annotation { "Feature Type Name" : "Feature", "Feature Type Description" : "" }
export const myFeature = defineFeature(function(context is Context, id is Id, definition is map)
    precondition{}
    {
        {
            var Q0;
            Q0=qCreatedBy(makeId("Front.planeOp"),FACE);
            var sketch = newSketch(context, id + "F0", { "sketchPlane" : qUnion([Q0])});
            skLineSegment(sketch, "E0.bottom", {"start": v(-5.31, 3.25) * mm, "end": v(8.02, 3.25) * mm});
            skLineSegment(sketch, "E0.top", {"start": v(-5.31, -3.25) * mm, "end": v(8.02, -3.25) * mm});
            skLineSegment(sketch, "E0.left", {"start": v(-5.31, 3.25) * mm, "end": v(-5.31, -3.25) * mm});
            skLineSegment(sketch, "E0.right", {"start": v(8.02, 3.25) * mm, "end": v(8.02, -3.25) * mm});
            skArc(sketch, "E1", {"start": v(-5.31, 3.25) * mm, "mid": v(-8.56, 0) * mm, "end": v(-5.31, -3.25) * mm});
            skArc(sketch, "E2", {"start": v(8.02, -3.25) * mm, "mid": v(11.27, 0) * mm, "end": v(8.02, 3.25) * mm});
            skLineSegment(sketch, "E3.0", {"start": v(-5.31, 5.26) * mm, "end": v(8.02, 5.26) * mm});
            skArc(sketch, "E3.1", {"start": v(-5.31, 5.26) * mm, "mid": v(-10.57, 0) * mm, "end": v(-5.31, -5.26) * mm});
            skLineSegment(sketch, "E3.2", {"start": v(-5.31, -5.26) * mm, "end": v(8.02, -5.26) * mm});
            skArc(sketch, "E3.3", {"start": v(8.02, -5.26) * mm, "mid": v(13.28, 0) * mm, "end": v(8.02, 5.26) * mm});
            skSolve(sketch);
        }
        {
            var Q0;
            Q0=makeQuery(id+"F0.imprint","IMPRINT",FACE,{"disambiguationData":[TD([[makeQuery(id+"F0.imprint","IMPRINT",EDGE,{"derivedFrom":sQuery(id+"F0.wireOp",EDGE,"E0.bottom")}),1.0]])]});
            extrude(context, id + "F1", {"entities" : qUnion([Q0]), "depth" : 55.88 * mm});
        }
        {
            var Q0;
            Q0=makeQuery(id+"F1.opExtrude","CAP_FACE",FACE,{"disambiguationData":[OSD([sQuery(id+"F0.wireOp",EDGE,"E0.bottom"),sQuery(id+"F0.wireOp",EDGE,"E0.top"),sQuery(id+"F0.wireOp",EDGE,"E1"),sQuery(id+"F0.wireOp",EDGE,"E2"),sQuery(id+"F0.wireOp",EDGE,"E3.0"),sQuery(id+"F0.wireOp",EDGE,"E3.1"),sQuery(id+"F0.wireOp",EDGE,"E3.2"),sQuery(id+"F0.wireOp",EDGE,"E3.3")])],"isStart":false});
            var sketch = newSketch(context, id + "F2", { "sketchPlane" : qUnion([Q0])});
            skLineSegment(sketch, "E4.bottom", {"start": v(-12.38, 7.2) * mm, "end": v(15.59, 7.2) * mm});
            skLineSegment(sketch, "E4.top", {"start": v(-12.38, 2.53) * mm, "end": v(15.59, 2.53) * mm});
            skLineSegment(sketch, "E4.left", {"start": v(-12.38, 7.2) * mm, "end": v(-12.38, 2.53) * mm});
            skLineSegment(sketch, "E4.right", {"start": v(15.59, 7.2) * mm, "end": v(15.59, 2.53) * mm});
            skSolve(sketch);
        }
        {
            var Q0;
            Q0 = qSketchRegion(id + "F2", true);
            extrude(context, id + "F3", {"entities" : qUnion([Q0]), "operationType" : NewBodyOperationType.REMOVE, "oppositeDirection" : true, "depth" : 55.88 * mm});
        }
        {
            var Q0;
            Q0=makeQuery(id+"F1.opExtrude","SWEPT_FACE",FACE,{"disambiguationData":[OSD([sQuery(id+"F0.wireOp",EDGE,"E3.2")])]});
            var sketch = newSketch(context, id + "F4", { "sketchPlane" : qUnion([Q0])});
            skText(sketch, "E5", { "text": "Vape Naysh", "fontName": "OpenSans-Regular.ttf"});
            const initialGuessF4  = {"E5": [-0.00178, 0.05391, 0, -1, 0.00668]};
            skSetInitialGuess(sketch, initialGuessF4);
            skSolve(sketch);
        }
        {
            var Q0;
            Q0 = qSketchRegion(id + "F4", true);
            extrude(context, id + "F5", {"entities" : qUnion([Q0]), "operationType" : NewBodyOperationType.REMOVE, "oppositeDirection" : true, "depth" : 25.4 * mm});
        }
        {
            var Q0;
            {var subQ1=sQuery(id+"F0.wireOp",EDGE,"E3.2");var subQ2=sQuery(id+"F0.wireOp",EDGE,"E3.1");Q0=makeQuery(id+"F5.boolean.opBoolean","SPLIT",FACE,{"disambiguationData":[TD([makeQuery(id+"F1.opExtrude","SWEPT_FACE",FACE,{"disambiguationData":[OSD([subQ2])]})])],"derivedFrom":makeQuery(id+"F1.opExtrude","SWEPT_FACE",FACE,{"disambiguationData":[OSD([subQ1])]})});}
            var sketch = newSketch(context, id + "F6", { "sketchPlane" : qUnion([Q0])});
            skLineSegment(sketch, "E6.bottom", {"start": v(1.17, 46.6) * mm, "end": v(-3.1, 46.6) * mm});
            skLineSegment(sketch, "E6.top", {"start": v(1.17, 46.39) * mm, "end": v(-3.1, 46.39) * mm});
            skLineSegment(sketch, "E6.left", {"start": v(1.17, 46.6) * mm, "end": v(1.17, 46.39) * mm});
            skLineSegment(sketch, "E6.right", {"start": v(-3.1, 46.6) * mm, "end": v(-3.1, 46.39) * mm});
            skFitSpline(sketch, "E7.0", {"points": [v(0.63, 45.49) * mm, v(0.6, 46.38) * mm, v(0.35, 46.78) * mm]});
            skFitSpline(sketch, "E8.0", {"points": [v(-1.03, 46.93) * mm, v(-1.25, 46.68) * mm, v(-1.25, 46.24) * mm]});
            skSolve(sketch);
        }
        {
            var Q0;
            {var subQ0=sQuery(id+"F6.wireOp",EDGE,"E7.0");var subQ1=sQuery(id+"F6.wireOp",EDGE,"E6.bottom");var subQ2=makeQuery(id+"F6.imprint","INTERSECT",VERTEX,{"derivedFrom":[subQ1,subQ0]});Q0=makeQuery(id+"F6.imprint","IMPRINT",FACE,{"disambiguationData":[TD([[makeQuery(id+"F6.imprint","IMPRINT",EDGE,{"disambiguationData":[TD([[subQ2,1.0]])],"derivedFrom":subQ1}),1.0]])]});}
            var Q1;
            {var subQ0=sQuery(id+"F6.wireOp",EDGE,"E8.0");var subQ1=sQuery(id+"F6.wireOp",EDGE,"E6.bottom");var subQ2=makeQuery(id+"F6.imprint","INTERSECT",VERTEX,{"derivedFrom":[subQ1,subQ0]});Q1=makeQuery(id+"F6.imprint","IMPRINT",FACE,{"disambiguationData":[TD([[makeQuery(id+"F6.imprint","IMPRINT",EDGE,{"disambiguationData":[TD([[subQ2,-1.0]])],"derivedFrom":subQ1}),1.0]])]});}
            var Q2;
            Q2=makeQuery(id+"F5.boolean.opBoolean","SPLIT",FACE,{"disambiguationData":[TD([makeQuery(id+"F5.opExtrude","SWEPT_FACE",FACE,{"disambiguationData":[OSD([sQuery(id+"F4.wireOp",EDGE,"E5.sketch_text.stroke-28")])]})])],"derivedFrom":makeQuery(id+"F1.opExtrude","SWEPT_FACE",FACE,{"disambiguationData":[OSD([sQuery(id+"F0.wireOp",EDGE,"E0.top")])]})});
            extrude(context, id + "F7", {"entities" : qUnion([Q0, Q1]), "operationType" : NewBodyOperationType.ADD, "endBound" : BoundingType.UP_TO_SURFACE, "oppositeDirection" : true, "endBoundEntityFace" : qUnion([Q2]), "depth" : 25.4 * mm});
        }
        {
            var Q0;
            Q0=makeQuery(id+"F5.boolean.opBoolean","SPLIT",FACE,{"disambiguationData":[TD([makeQuery(id+"F5.opExtrude","SWEPT_FACE",FACE,{"disambiguationData":[OSD([sQuery(id+"F4.wireOp",EDGE,"E5.sketch_text.stroke-52")])]})])],"derivedFrom":makeQuery(id+"F1.opExtrude","SWEPT_FACE",FACE,{"disambiguationData":[OSD([sQuery(id+"F0.wireOp",EDGE,"E3.2")])]})});
            var sketch = newSketch(context, id + "F8", { "sketchPlane" : qUnion([Q0])});
            skLineSegment(sketch, "E9.bottom", {"start": v(3.44, 40.97) * mm, "end": v(-2.3, 40.97) * mm});
            skLineSegment(sketch, "E9.top", {"start": v(3.44, 40.66) * mm, "end": v(-2.3, 40.66) * mm});
            skLineSegment(sketch, "E9.left", {"start": v(3.44, 40.97) * mm, "end": v(3.44, 40.66) * mm});
            skLineSegment(sketch, "E9.right", {"start": v(-2.3, 40.97) * mm, "end": v(-2.3, 40.66) * mm});
            skSolve(sketch);
        }
        {
            var Q0;
            {var subQ0=sQuery(id+"F8.wireOp",EDGE,"E9.right");Q0=makeQuery(id+"F8.imprint","IMPRINT",FACE,{"disambiguationData":[TD([[makeQuery(id+"F8.imprint","IMPRINT",EDGE,{"derivedFrom":subQ0}),1.0]])]});}
            var Q1;
            {var subQ0=sQuery(id+"F8.wireOp",EDGE,"E9.left");Q1=makeQuery(id+"F8.imprint","IMPRINT",FACE,{"disambiguationData":[TD([[makeQuery(id+"F8.imprint","IMPRINT",EDGE,{"derivedFrom":subQ0}),-1.0]])]});}
            extrude(context, id + "F9", {"entities" : qUnion([Q0, Q1]), "operationType" : NewBodyOperationType.ADD, "oppositeDirection" : true, "depth" : 2 * mm});
        }
        {
            var Q0;
            {var subQ0=sQuery(id+"F4.wireOp",EDGE,"E5.sketch_text.stroke-68");var subQ1=sQuery(id+"F4.wireOp",EDGE,"E5.sketch_text.stroke-65");var subQ2=sQuery(id+"F4.wireOp",EDGE,"E5.sketch_text.stroke-64");var subQ3=sQuery(id+"F8.wireOp",EDGE,"E9.top");var subQ4=sQuery(id+"F8.wireOp",EDGE,"E9.bottom");var subQ5=sQuery(id+"F4.wireOp",EDGE,"E5.sketch_text.stroke-56");var subQ6=sQuery(id+"F4.wireOp",EDGE,"E5.sketch_text.stroke-52");var subQ7=sQuery(id+"F6.wireOp",EDGE,"E6.top");var subQ8=sQuery(id+"F6.wireOp",EDGE,"E6.bottom");var subQ9=sQuery(id+"F4.wireOp",EDGE,"E5.sketch_text.stroke-13");var subQ10=sQuery(id+"F4.wireOp",EDGE,"E5.sketch_text.stroke-15");var subQ11=sQuery(id+"F0.wireOp",EDGE,"E3.2");var subQ12=makeQuery(id+"F1.opExtrude","SWEPT_FACE",FACE,{"disambiguationData":[OSD([subQ11])]});var subQ14=sQuery(id+"F0.wireOp",EDGE,"E3.1");Q0=makeQuery(id+"FvCUFkXDUsI6DTU_1.boolean.opBoolean","MERGE",FACE,{"derivedFrom":[makeQuery(id+"F5.boolean.opBoolean","SPLIT",FACE,{"disambiguationData":[TD([makeQuery(id+"F5.opExtrude","SWEPT_FACE",FACE,{"disambiguationData":[OSD([sQuery(id+"F4.wireOp",EDGE,"E5.sketch_text.stroke-75")])]})])],"derivedFrom":subQ12}),makeQuery(id+"F9.boolean.opBoolean","MERGE",FACE,{"derivedFrom":[makeQuery(id+"F5.boolean.opBoolean","SPLIT",FACE,{"disambiguationData":[TD([makeQuery(id+"F5.opExtrude","SWEPT_FACE",FACE,{"disambiguationData":[OSD([subQ6])]})])],"derivedFrom":subQ12}),makeQuery(id+"F7.boolean.opBoolean","MERGE",FACE,{"derivedFrom":[makeQuery(id+"F5.boolean.opBoolean","SPLIT",FACE,{"disambiguationData":[TD([makeQuery(id+"F1.opExtrude","SWEPT_FACE",FACE,{"disambiguationData":[OSD([subQ14])]})])],"derivedFrom":subQ12}),makeQuery(id+"F5.boolean.opBoolean","SPLIT",FACE,{"disambiguationData":[TD([makeQuery(id+"F5.opExtrude","SWEPT_FACE",FACE,{"disambiguationData":[OSD([sQuery(id+"F4.wireOp",EDGE,"E5.sketch_text.stroke-28")])]})])],"derivedFrom":subQ12}),makeQuery(id+"F7.opExtrude","CAP_FACE",FACE,{"disambiguationData":[OSD([subQ10,subQ8,subQ7,sQuery(id+"F6.wireOp",EDGE,"E7.0")])],"isStart":true}),makeQuery(id+"F7.opExtrude","CAP_FACE",FACE,{"disambiguationData":[OSD([subQ9,subQ8,subQ7,sQuery(id+"F6.wireOp",EDGE,"E8.0")])],"isStart":true})]}),makeQuery(id+"F9.opExtrude","CAP_FACE",FACE,{"disambiguationData":[OSD([subQ6,subQ4,subQ3,sQuery(id+"F8.wireOp",EDGE,"E9.left")])],"isStart":true}),makeQuery(id+"F9.opExtrude","CAP_FACE",FACE,{"disambiguationData":[OSD([subQ5,subQ4,subQ3,sQuery(id+"F8.wireOp",EDGE,"E9.right")])],"isStart":true})]}),makeQuery(id+"FvCUFkXDUsI6DTU_1.opExtrude","CAP_FACE",FACE,{"disambiguationData":[OSD([subQ2,subQ1,subQ0,sQuery(id+"FhZDdOnHOzzq7TN_1.wireOp",EDGE,"bsYgK6K2-3tY7-JA5x-VERg-xGbtDLP8pClo.bottom"),sQuery(id+"FhZDdOnHOzzq7TN_1.wireOp",EDGE,"bsYgK6K2-3tY7-JA5x-VERg-xGbtDLP8pClo.top")])],"isStart":true})]});}
            var sketch = newSketch(context, id + "F10", { "sketchPlane" : qUnion([Q0])});
            skLineSegment(sketch, "E10.bottom", {"start": v(1.56, 20.76) * mm, "end": v(-2.41, 20.76) * mm});
            skLineSegment(sketch, "E10.top", {"start": v(1.56, 20.47) * mm, "end": v(-2.41, 20.47) * mm});
            skLineSegment(sketch, "E10.left", {"start": v(1.56, 20.76) * mm, "end": v(1.56, 20.47) * mm});
            skLineSegment(sketch, "E10.right", {"start": v(-2.41, 20.76) * mm, "end": v(-2.41, 20.47) * mm});
            skSolve(sketch);
        }
        {
            var Q0;
            {var subQ0=sQuery(id+"F10.wireOp",EDGE,"E10.bottom");var subQ1=makeQuery(id+"F5.boolean.opBoolean","COPY",EDGE,{"derivedFrom":makeQuery(id+"F5.opExtrude","CAP_EDGE",EDGE,{"disambiguationData":[OSD([sQuery(id+"F4.wireOp",EDGE,"E5.sketch_text.stroke-101")])],"isStart":true})});var subQ2=makeQuery(id+"F10.imprint","INTERSECT",VERTEX,{"derivedFrom":[subQ1,subQ0]});Q0=makeQuery(id+"F10.imprint","IMPRINT",FACE,{"disambiguationData":[TD([[makeQuery(id+"F10.imprint","IMPRINT",EDGE,{"disambiguationData":[TD([[subQ2,-1.0]])],"derivedFrom":subQ0}),1.0]])]});}
            extrude(context, id + "F11", {"entities" : qUnion([Q0]), "operationType" : NewBodyOperationType.ADD, "oppositeDirection" : true, "depth" : 2 * mm});
        }
        {
            var Q0;
            {var subQ0=sQuery(id+"F4.wireOp",EDGE,"E5.sketch_text.stroke-101");var subQ1=sQuery(id+"F4.wireOp",EDGE,"E5.sketch_text.stroke-98");var subQ2=sQuery(id+"F8.wireOp",EDGE,"E9.top");var subQ3=sQuery(id+"F8.wireOp",EDGE,"E9.bottom");var subQ4=sQuery(id+"F4.wireOp",EDGE,"E5.sketch_text.stroke-56");var subQ5=sQuery(id+"F4.wireOp",EDGE,"E5.sketch_text.stroke-52");var subQ6=sQuery(id+"F6.wireOp",EDGE,"E6.top");var subQ7=sQuery(id+"F6.wireOp",EDGE,"E6.bottom");var subQ8=sQuery(id+"F4.wireOp",EDGE,"E5.sketch_text.stroke-13");var subQ9=sQuery(id+"F4.wireOp",EDGE,"E5.sketch_text.stroke-15");var subQ10=sQuery(id+"F0.wireOp",EDGE,"E3.2");var subQ11=makeQuery(id+"F1.opExtrude","SWEPT_FACE",FACE,{"disambiguationData":[OSD([subQ10])]});var subQ13=sQuery(id+"F0.wireOp",EDGE,"E3.1");Q0=makeQuery(id+"F11.boolean.opBoolean","MERGE",FACE,{"derivedFrom":[makeQuery(id+"F5.boolean.opBoolean","SPLIT",FACE,{"disambiguationData":[TD([makeQuery(id+"F5.opExtrude","SWEPT_FACE",FACE,{"disambiguationData":[OSD([sQuery(id+"F4.wireOp",EDGE,"E5.sketch_text.stroke-114")])]})])],"derivedFrom":subQ11}),makeQuery(id+"F9.boolean.opBoolean","MERGE",FACE,{"derivedFrom":[makeQuery(id+"F5.boolean.opBoolean","SPLIT",FACE,{"disambiguationData":[TD([makeQuery(id+"F5.opExtrude","SWEPT_FACE",FACE,{"disambiguationData":[OSD([subQ5])]})])],"derivedFrom":subQ11}),makeQuery(id+"F7.boolean.opBoolean","MERGE",FACE,{"derivedFrom":[makeQuery(id+"F5.boolean.opBoolean","SPLIT",FACE,{"disambiguationData":[TD([makeQuery(id+"F1.opExtrude","SWEPT_FACE",FACE,{"disambiguationData":[OSD([subQ13])]})])],"derivedFrom":subQ11}),makeQuery(id+"F5.boolean.opBoolean","SPLIT",FACE,{"disambiguationData":[TD([makeQuery(id+"F5.opExtrude","SWEPT_FACE",FACE,{"disambiguationData":[OSD([sQuery(id+"F4.wireOp",EDGE,"E5.sketch_text.stroke-28")])]})])],"derivedFrom":subQ11}),makeQuery(id+"F7.opExtrude","CAP_FACE",FACE,{"disambiguationData":[OSD([subQ9,subQ7,subQ6,sQuery(id+"F6.wireOp",EDGE,"E7.0")])],"isStart":true}),makeQuery(id+"F7.opExtrude","CAP_FACE",FACE,{"disambiguationData":[OSD([subQ8,subQ7,subQ6,sQuery(id+"F6.wireOp",EDGE,"E8.0")])],"isStart":true})]}),makeQuery(id+"F9.opExtrude","CAP_FACE",FACE,{"disambiguationData":[OSD([subQ5,subQ3,subQ2,sQuery(id+"F8.wireOp",EDGE,"E9.left")])],"isStart":true}),makeQuery(id+"F9.opExtrude","CAP_FACE",FACE,{"disambiguationData":[OSD([subQ4,subQ3,subQ2,sQuery(id+"F8.wireOp",EDGE,"E9.right")])],"isStart":true})]}),makeQuery(id+"F11.opExtrude","CAP_FACE",FACE,{"disambiguationData":[OSD([subQ1,subQ0,sQuery(id+"F10.wireOp",EDGE,"E10.bottom"),sQuery(id+"F10.wireOp",EDGE,"E10.top")])],"isStart":true})]});}
            var sketch = newSketch(context, id + "F12", { "sketchPlane" : qUnion([Q0])});
            skLineSegment(sketch, "E11.bottom", {"start": v(3.54, 35.07) * mm, "end": v(-0.16, 35.07) * mm});
            skLineSegment(sketch, "E11.top", {"start": v(3.54, 34.84) * mm, "end": v(-0.16, 34.84) * mm});
            skLineSegment(sketch, "E11.left", {"start": v(3.54, 35.07) * mm, "end": v(3.54, 34.84) * mm});
            skLineSegment(sketch, "E11.right", {"start": v(-0.16, 35.07) * mm, "end": v(-0.16, 34.84) * mm});
            skSolve(sketch);
        }
        {
            var Q0;
            Q0 = qSketchRegion(id + "F12", true);
            extrude(context, id + "F13", {"entities" : qUnion([Q0]), "operationType" : NewBodyOperationType.ADD, "oppositeDirection" : true, "depth" : 2 * mm});
        }
    });